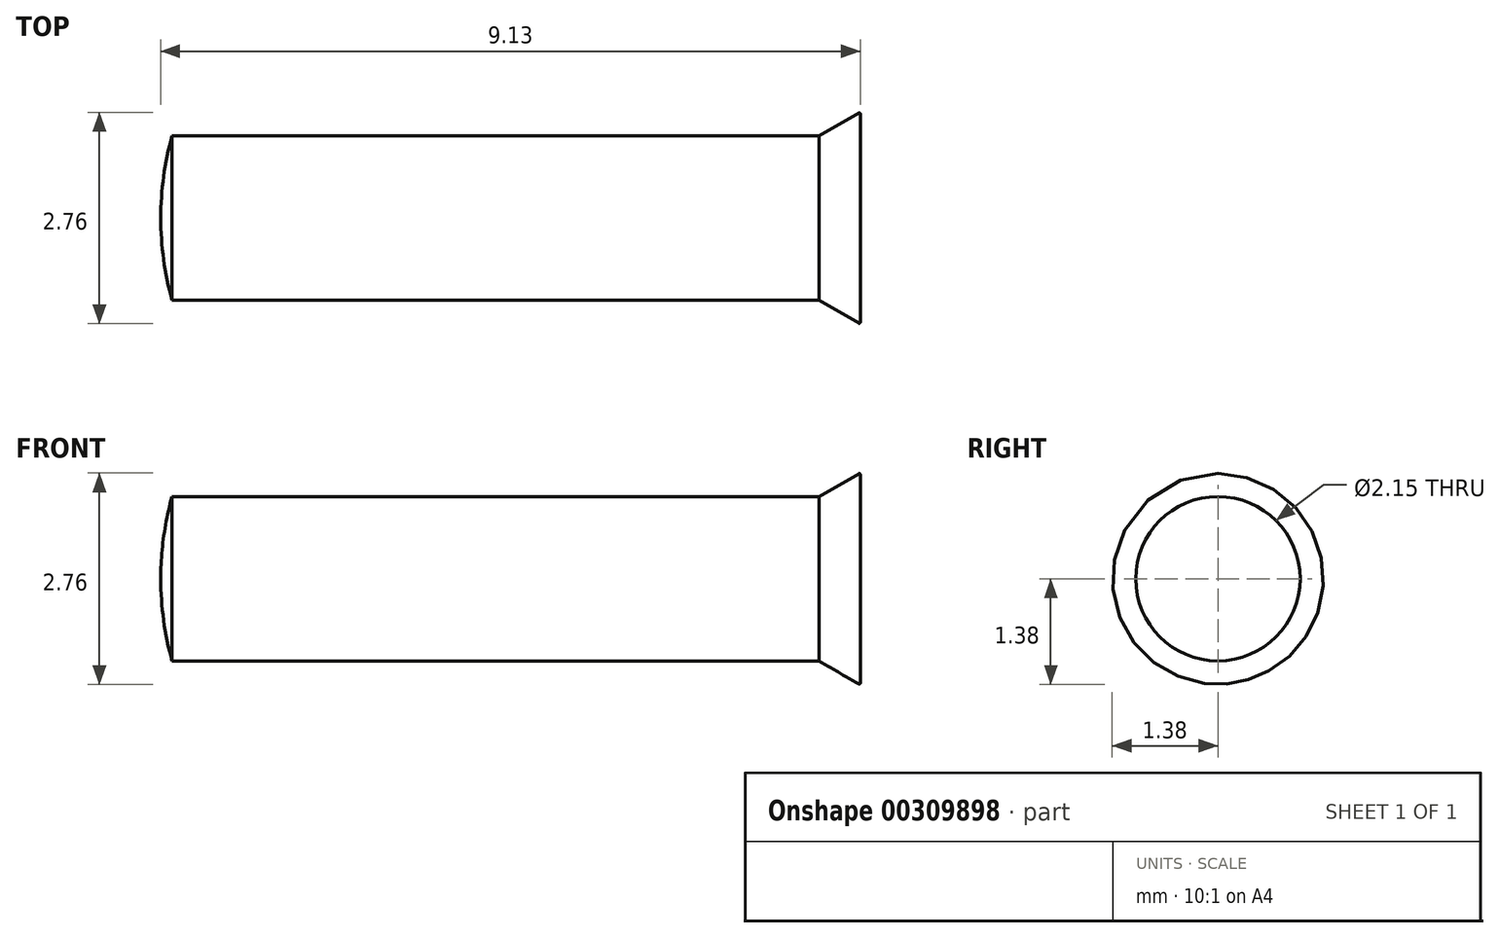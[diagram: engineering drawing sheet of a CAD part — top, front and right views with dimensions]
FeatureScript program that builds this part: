
annotation { "Feature Type Name" : "Feature", "Feature Type Description" : "" }
export const myFeature = defineFeature(function(context is Context, id is Id, definition is map)
    precondition{}
    {
        {
            var Q0;
            Q0=qCreatedBy(makeId("Front.planeOp"),FACE);
            var sketch = newSketch(context, id + "F0", { "sketchPlane" : qUnion([Q0])});
            skLineSegment(sketch, "E0", {"start": v(0, 0) * mm, "end": v(-9.13, 0) * mm});
            skLineSegment(sketch, "E1", {"start": v(-9.13, 0) * mm, "end": v(-9.13, 1.07) * mm, "construction": true});
            skLineSegment(sketch, "E2", {"start": v(-8.98, 1.07) * mm, "end": v(-0.54, 1.07) * mm});
            skLineSegment(sketch, "E3", {"start": v(-0.54, 1.07) * mm, "end": v(0, 1.38) * mm});
            skLineSegment(sketch, "E4", {"start": v(0, 1.38) * mm, "end": v(0, 0) * mm});
            skArc(sketch, "E5", {"start": v(-9.13, 0) * mm, "mid": v(-9.1, 0.54) * mm, "end": v(-8.98, 1.07) * mm});
            skSolve(sketch);
        }
        {
            var Q0;
            Q0=sQuery(id+"F0.wireOp",EDGE,"E5");
            var Q1;
            Q1=sQuery(id+"F0.wireOp",EDGE,"E2");
            var Q2;
            Q2=sQuery(id+"F0.wireOp",EDGE,"E3");
            var Q3;
            Q3=sQuery(id+"F0.wireOp",EDGE,"E4");
            var Q4;
            Q4=sQuery(id+"F0.wireOp",EDGE,"E0");
            revolve(context, id + "F1", {"bodyType" : ToolBodyType.SURFACE, "surfaceEntities" : qUnion([Q0, Q1, Q2, Q3]), "axis" : qUnion([Q4]), "revolveType" : RevolveType.FULL});
        }
        {
            var Q0;
            Q0=makeQuery(id+"F1.opRevolve","SWEPT_EDGE",EDGE,{"disambiguationData":[OSD([sQuery(id+"F0.wireOp",VERTEX,"E4.start")])]});
            fillet(context, id + "F2", {"entities" : qUnion([Q0]), "radius" : 0.01 * mm, "tangentPropagation" : true, "allowEdgeOverflow" : false});
        }
    });
